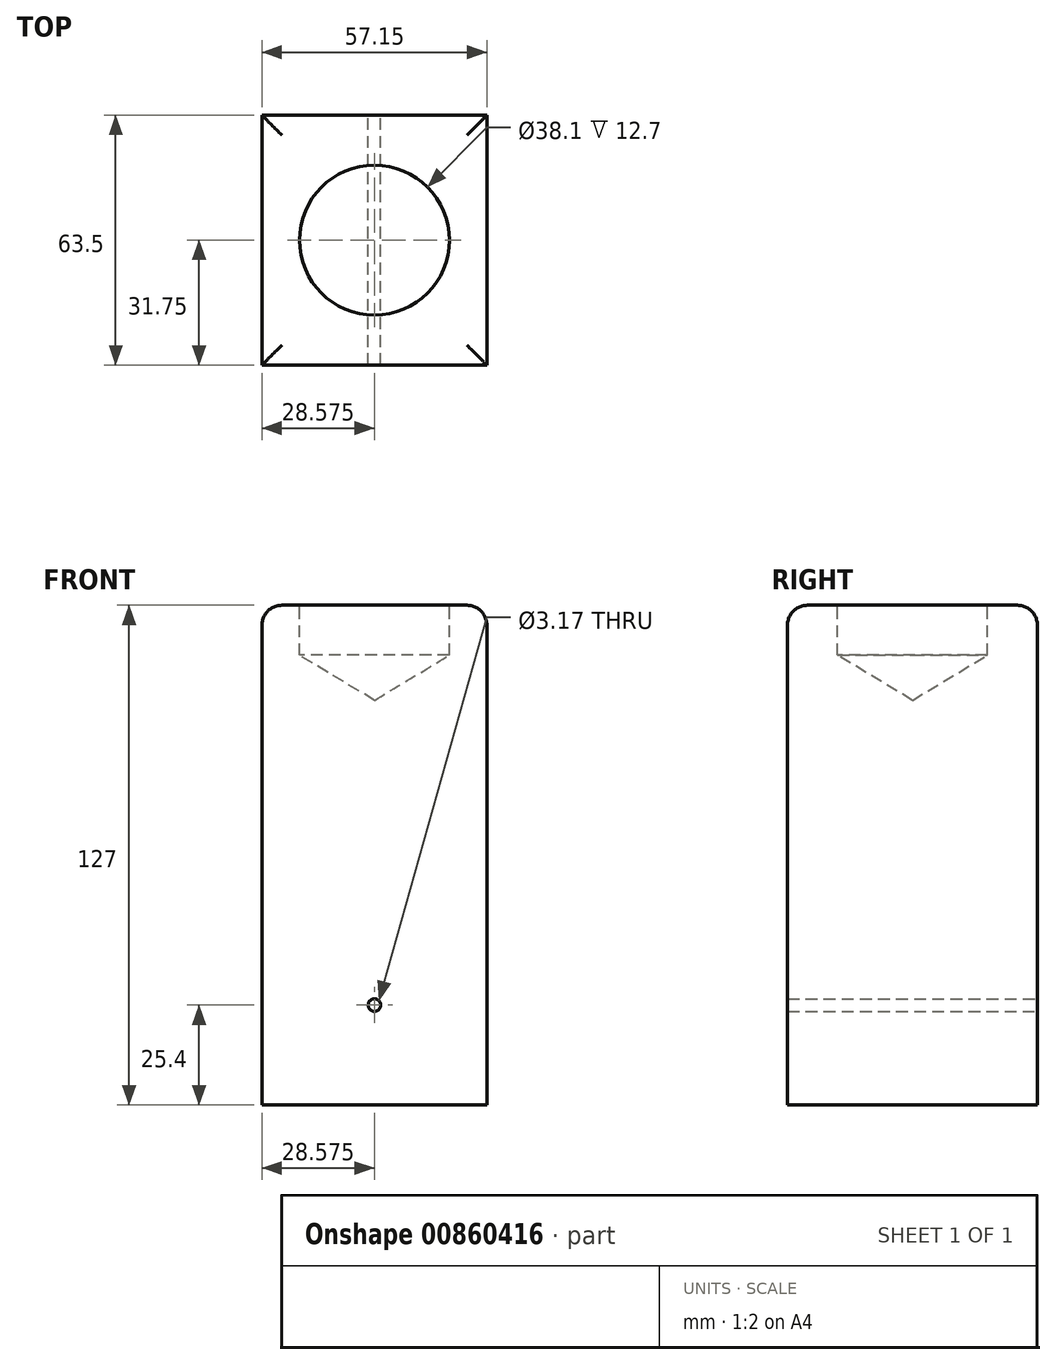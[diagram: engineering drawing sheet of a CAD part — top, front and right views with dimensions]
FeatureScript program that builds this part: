
annotation { "Feature Type Name" : "Feature", "Feature Type Description" : "" }
export const myFeature = defineFeature(function(context is Context, id is Id, definition is map)
    precondition{}
    {
        {
            var Q0;
            Q0=qCreatedBy(makeId("Top.planeOp"),FACE);
            var sketch = newSketch(context, id + "F0", { "sketchPlane" : qUnion([Q0])});
            skLineSegment(sketch, "E0.bottom", {"start": v(0, 0) * mm, "end": v(57.15, 0) * mm});
            skLineSegment(sketch, "E0.top", {"start": v(0, -63.5) * mm, "end": v(57.15, -63.5) * mm});
            skLineSegment(sketch, "E0.left", {"start": v(0, 0) * mm, "end": v(0, -63.5) * mm});
            skLineSegment(sketch, "E0.right", {"start": v(57.15, 0) * mm, "end": v(57.15, -63.5) * mm});
            skSolve(sketch);
        }
        {
            var Q0;
            Q0=makeQuery(id+"F0.imprint","IMPRINT",FACE,{"disambiguationData":[TD([[makeQuery(id+"F0.imprint","IMPRINT",EDGE,{"derivedFrom":sQuery(id+"F0.wireOp",EDGE,"E0.bottom")}),-1.0]])]});
            extrude(context, id + "F1", {"entities" : qUnion([Q0]), "depth" : 127 * mm, "offsetDistance" : 25.4 * mm});
        }
        {
            var Q0;
            Q0=makeQuery(id+"F1.opExtrude","CAP_FACE",FACE,{"disambiguationData":[OSD([sQuery(id+"F0.wireOp",EDGE,"E0.bottom"),sQuery(id+"F0.wireOp",EDGE,"E0.top"),sQuery(id+"F0.wireOp",EDGE,"E0.left"),sQuery(id+"F0.wireOp",EDGE,"E0.right")])],"isStart":false});
            var sketch = newSketch(context, id + "F2", { "sketchPlane" : qUnion([Q0])});
            skLineSegment(sketch, "E1", {"start": v(28.58, 0) * mm, "end": v(28.58, -63.5) * mm, "construction": true});
            skLineSegment(sketch, "E2", {"start": v(0, -31.75) * mm, "end": v(57.15, -31.75) * mm, "construction": true});
            skPoint(sketch, "E3", {"position": v(28.58, -31.75) * mm});
            skSolve(sketch);
        }
        {
            var Q0;
            Q0=sQuery(id+"F2.wireOp",VERTEX,"E3");
            var Q1;
            Q1=makeQuery(id+"F1.opExtrude","SWEPT_BODY",BODY,{"disambiguationData":[OSD([sQuery(id+"F0.wireOp",EDGE,"E0.bottom"),sQuery(id+"F0.wireOp",EDGE,"E0.top"),sQuery(id+"F0.wireOp",EDGE,"E0.left"),sQuery(id+"F0.wireOp",EDGE,"E0.right")])]});
            hole(context, id + "F3", {"style" : HoleStyle.SIMPLE, "endStyle" : HoleEndStyle.BLIND, "holeDiameter" : 38.1 * mm, "majorDiameter" : 6.35 * mm, "holeDepth" : 12.7 * mm, "isTappedThrough" : true, "tappedDepth" : 12.7 * mm, "tapClearance" : 3, "locations" : qUnion([Q0]), "scope" : qUnion([Q1])});
        }
        {
            var Q0;
            Q0=makeQuery(id+"F1.opExtrude","CAP_EDGE",EDGE,{"disambiguationData":[OSD([sQuery(id+"F0.wireOp",EDGE,"E0.right")])],"isStart":false});
            var Q1;
            Q1=makeQuery(id+"F1.opExtrude","CAP_EDGE",EDGE,{"disambiguationData":[OSD([sQuery(id+"F0.wireOp",EDGE,"E0.bottom")])],"isStart":false});
            var Q2;
            Q2=makeQuery(id+"F1.opExtrude","CAP_EDGE",EDGE,{"disambiguationData":[OSD([sQuery(id+"F0.wireOp",EDGE,"E0.left")])],"isStart":false});
            var Q3;
            Q3=makeQuery(id+"F1.opExtrude","CAP_EDGE",EDGE,{"disambiguationData":[OSD([sQuery(id+"F0.wireOp",EDGE,"E0.top")])],"isStart":false});
            fillet(context, id + "F4", {"entities" : qUnion([Q0, Q1, Q2, Q3]), "radius" : 5.08 * mm, "tangentPropagation" : true, "allowEdgeOverflow" : false});
        }
        {
            var Q0;
            Q0=makeQuery(id+"F1.opExtrude","SWEPT_FACE",FACE,{"disambiguationData":[OSD([sQuery(id+"F0.wireOp",EDGE,"E0.bottom")])]});
            var sketch = newSketch(context, id + "F5", { "sketchPlane" : qUnion([Q0])});
            skPoint(sketch, "E4", {"position": v(-28.58, 25.4) * mm});
            skSolve(sketch);
        }
        {
            var Q0;
            Q0=sQuery(id+"F5.wireOp",VERTEX,"E4");
            var Q1;
            Q1=makeQuery(id+"F1.opExtrude","SWEPT_BODY",BODY,{"disambiguationData":[OSD([sQuery(id+"F0.wireOp",EDGE,"E0.bottom"),sQuery(id+"F0.wireOp",EDGE,"E0.top"),sQuery(id+"F0.wireOp",EDGE,"E0.left"),sQuery(id+"F0.wireOp",EDGE,"E0.right")])]});
            hole(context, id + "F6", {"style" : HoleStyle.SIMPLE, "endStyle" : HoleEndStyle.THROUGH, "holeDiameter" : 3.17 * mm, "majorDiameter" : 6.35 * mm, "isTappedThrough" : true, "tappedDepth" : 12.7 * mm, "tapClearance" : 3, "locations" : qUnion([Q0]), "scope" : qUnion([Q1])});
        }
    });
